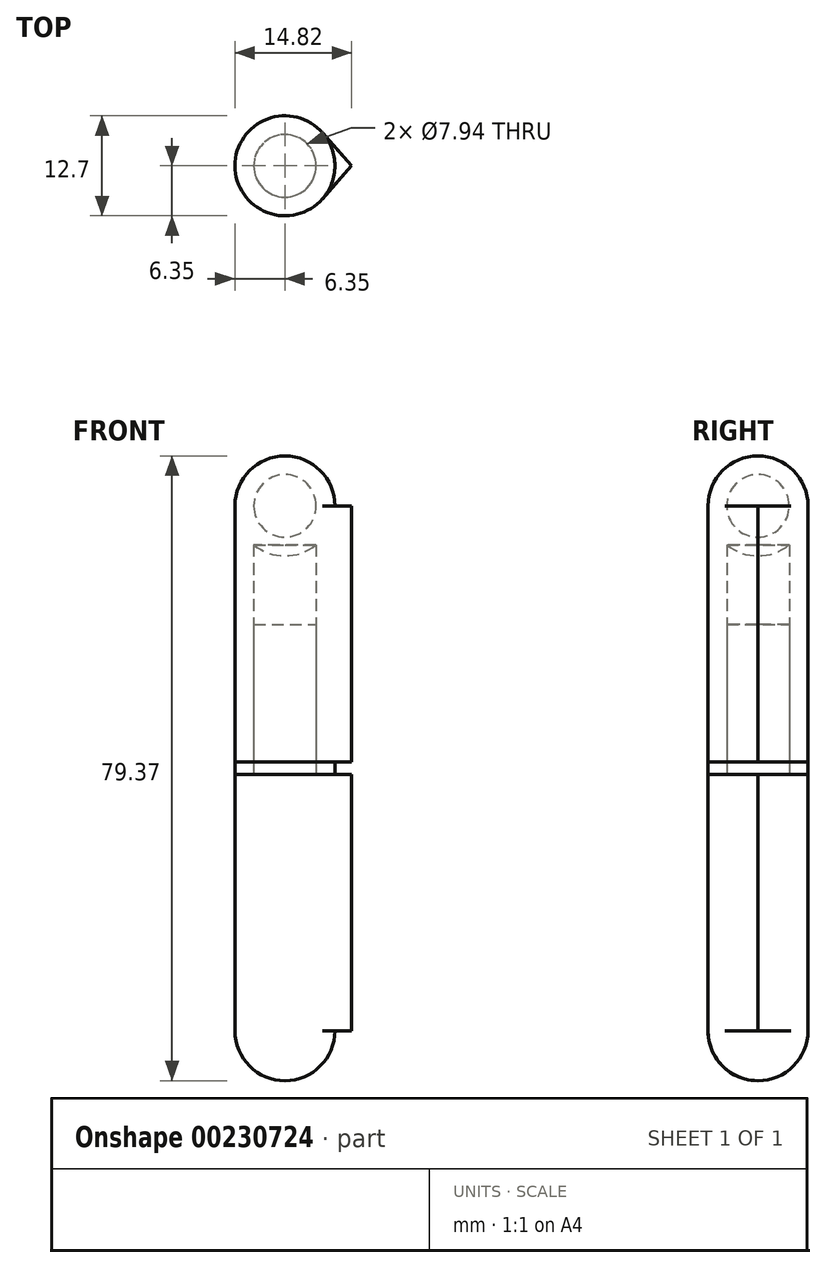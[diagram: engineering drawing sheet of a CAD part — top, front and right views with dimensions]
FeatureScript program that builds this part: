
annotation { "Feature Type Name" : "Feature", "Feature Type Description" : "" }
export const myFeature = defineFeature(function(context is Context, id is Id, definition is map)
    precondition{}
    {
        {
            var Q0;
            Q0=qCreatedBy(makeId("Top.planeOp"),FACE);
            var sketch = newSketch(context, id + "F0", { "sketchPlane" : qUnion([Q0])});
            skCircle(sketch, "E0", {"center": v(0, 0) * mm, "radius": 6.35 * mm});
            skLineSegment(sketch, "E1", {"start": v(8.47, 0) * mm, "end": v(4.76, 4.2) * mm});
            skLineSegment(sketch, "E2", {"start": v(8.47, 0) * mm, "end": v(4.76, -4.2) * mm});
            skSolve(sketch);
        }
        {
            var Q0;
            Q0=qCreatedBy(makeId("Right.planeOp"),FACE);
            var sketch = newSketch(context, id + "F1", { "sketchPlane" : qUnion([Q0])});
            skArc(sketch, "E3", {"start": v(6.35, 0) * mm, "mid": v(4.5, 4.5) * mm, "end": v(0, 6.35) * mm});
            skLineSegment(sketch, "E4", {"start": v(0, 0) * mm, "end": v(6.35, 0) * mm});
            skLineSegment(sketch, "E5", {"start": v(0, 0) * mm, "end": v(0, 6.35) * mm});
            skSolve(sketch);
        }
        {
            var Q0;
            Q0=qSketchRegion(id+"F1",true);
            var Q1;
            Q1=sQuery(id+"F1.wireOp",EDGE,"E5");
            revolve(context, id + "F2", {"entities" : qUnion([Q0]), "axis" : qUnion([Q1]), "revolveType" : RevolveType.FULL});
        }
        {
            var Q0;
            Q0=qSketchRegion(id+"F0",true);
            extrude(context, id + "F3", {"entities" : qUnion([Q0]), "operationType" : NewBodyOperationType.ADD, "oppositeDirection" : true, "depth" : 32.54 * mm});
        }
        {
            var Q0;
            Q0=makeQuery(id+"F3.opExtrude","CAP_FACE",FACE,{"disambiguationData":[OSD([sQuery(id+"F0.wireOp",EDGE,"E0"),sQuery(id+"F0.wireOp",EDGE,"E1"),sQuery(id+"F0.wireOp",EDGE,"E2")])],"isStart":false});
            var sketch = newSketch(context, id + "F4", { "sketchPlane" : qUnion([Q0])});
            skCircle(sketch, "E6", {"center": v(0, 0) * mm, "radius": 3.97 * mm});
            skSolve(sketch);
        }
        {
            var Q0;
            Q0=qSketchRegion(id+"F4",true);
            extrude(context, id + "F5", {"entities" : qUnion([Q0]), "operationType" : NewBodyOperationType.ADD, "depth" : 19.05 * mm});
        }
        {
            var Q0;
            Q0=qCreatedBy(makeId("Top.planeOp"),FACE);
            var sketch = newSketch(context, id + "F6", { "sketchPlane" : qUnion([Q0])});
            skLineSegment(sketch, "E7", {"start": v(0, 0) * mm, "end": v(-57.87, 0) * mm});
            skSolve(sketch);
        }
        {
            var Q0;
            Q0=makeQuery(id+"F2.opRevolve","SWEPT_BODY",BODY,{"disambiguationData":[OSD([sQuery(id+"F1.wireOp",EDGE,"E3"),sQuery(id+"F1.wireOp",EDGE,"E4"),sQuery(id+"F1.wireOp",EDGE,"E5")])]});
            var Q1;
            Q1=sQuery(id+"F6.wireOp",EDGE,"E7");
            transform(context, id + "F7", {"entities" : qUnion([Q0]), "transformType" : TransformType.ROTATION, "transformAxis" : qUnion([Q1]), "angle" : 180 * degree, "makeCopy" : false});
        }
        {
            var Q0;
            Q0=makeQuery(id+"F2.opRevolve","SWEPT_BODY",BODY,{"disambiguationData":[OSD([sQuery(id+"F1.wireOp",EDGE,"E3"),sQuery(id+"F1.wireOp",EDGE,"E4"),sQuery(id+"F1.wireOp",EDGE,"E5")])]});
            transform(context, id + "F8", {"entities" : qUnion([Q0]), "transformType" : TransformType.TRANSLATION_3D, "dx" : 0 * mm, "dy" : 0 * mm, "dz" : 0 * mm, "makeCopy" : true});
        }
        {
            var Q0;
            Q0=makeQuery(id+"F8.opPattern","COPY",BODY,{"derivedFrom":makeQuery(id+"F2.opRevolve","SWEPT_BODY",BODY,{"disambiguationData":[OSD([sQuery(id+"F1.wireOp",EDGE,"E3"),sQuery(id+"F1.wireOp",EDGE,"E4"),sQuery(id+"F1.wireOp",EDGE,"E5")])]}),"instanceName":"1"});
            deleteBodies(context, id + "F9", {"entities" : qUnion([Q0])});
        }
        {
            var Q0;
            Q0=makeQuery(id+"F3.opExtrude","CAP_FACE",FACE,{"disambiguationData":[OSD([sQuery(id+"F0.wireOp",EDGE,"E0"),sQuery(id+"F0.wireOp",EDGE,"E1"),sQuery(id+"F0.wireOp",EDGE,"E2")])],"isStart":false});
            var sketch = newSketch(context, id + "F10", { "sketchPlane" : qUnion([Q0])});
            skCircle(sketch, "E8", {"center": v(0, 0) * mm, "radius": 3.97 * mm});
            skCircle(sketch, "E9", {"center": v(0, 0) * mm, "radius": 6.35 * mm});
            skSolve(sketch);
        }
        {
            var Q0;
            Q0 = qSketchRegion(id + "F10", true);
            extrude(context, id + "F11", {"entities" : qUnion([Q0]), "depth" : 1.59 * mm});
        }
        {
            var Q0;
            Q0=makeQuery(id+"F11.opExtrude","CAP_FACE",FACE,{"disambiguationData":[OSD([sQuery(id+"F10.wireOp",EDGE,"E8"),sQuery(id+"F10.wireOp",EDGE,"E9")])],"isStart":false});
            var sketch = newSketch(context, id + "F12", { "sketchPlane" : qUnion([Q0])});
            skCircle(sketch, "E10", {"center": v(0, 0) * mm, "radius": 3.97 * mm});
            skCircle(sketch, "E11", {"center": v(0, 0) * mm, "radius": 6.35 * mm});
            skLineSegment(sketch, "E12", {"start": v(8.44, 0) * mm, "end": v(4.78, 4.18) * mm});
            skLineSegment(sketch, "E13", {"start": v(8.44, 0) * mm, "end": v(4.78, -4.18) * mm});
            skSolve(sketch);
        }
        {
            var Q0;
            {var subQ0=sQuery(id+"F12.wireOp",EDGE,"E12");Q0=makeQuery(id+"F12.imprint","IMPRINT",FACE,{"disambiguationData":[TD([[makeQuery(id+"F12.imprint","IMPRINT",EDGE,{"derivedFrom":subQ0}),1.0]])]});}
            var Q1;
            Q1=makeQuery(id+"F12.imprint","IMPRINT",FACE,{"disambiguationData":[TD([[makeQuery(id+"F12.imprint","IMPRINT",EDGE,{"derivedFrom":sQuery(id+"F12.wireOp",EDGE,"E10")}),-1.0]])]});
            extrude(context, id + "F13", {"entities" : qUnion([Q0, Q1]), "depth" : 32.54 * mm});
        }
        {
            var Q0;
            Q0=makeQuery(id+"F13.opExtrude","CAP_FACE",FACE,{"disambiguationData":[OSD([sQuery(id+"F12.wireOp",EDGE,"E10"),sQuery(id+"F12.wireOp",EDGE,"E11"),sQuery(id+"F12.wireOp",EDGE,"E12"),sQuery(id+"F12.wireOp",EDGE,"E13")])],"isStart":false});
            var sketch = newSketch(context, id + "F14", { "sketchPlane" : qUnion([Q0])});
            skArc(sketch, "E14", {"start": v(6.35, 0) * mm, "mid": v(0, 6.35) * mm, "end": v(-6.35, 0) * mm});
            skLineSegment(sketch, "E15", {"start": v(6.35, 0) * mm, "end": v(-6.35, 0) * mm});
            skSolve(sketch);
        }
        {
            var Q0;
            {var subQ1=sQuery(id+"F14.wireOp",EDGE,"E14");var subQ7=makeQuery(id+"F14.imprint","INTERSECT",VERTEX,{"derivedFrom":[makeQuery(id+"F13.opExtrude","CAP_EDGE",EDGE,{"disambiguationData":[OSD([sQuery(id+"F12.wireOp",EDGE,"E12")])],"isStart":false}),subQ1]});Q0=makeQuery(id+"F14.imprint","IMPRINT",FACE,{"disambiguationData":[TD([[makeQuery(id+"F14.imprint","IMPRINT",EDGE,{"disambiguationData":[TD([[subQ7,1.0]])],"derivedFrom":subQ1}),1.0]])]});}
            var Q1;
            Q1=sQuery(id+"F14.wireOp",EDGE,"E15");
            revolve(context, id + "F15", {"operationType" : NewBodyOperationType.ADD, "entities" : qUnion([Q0]), "axis" : qUnion([Q1]), "revolveType" : RevolveType.FULL});
        }
    });
